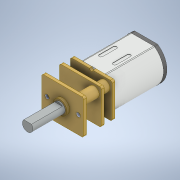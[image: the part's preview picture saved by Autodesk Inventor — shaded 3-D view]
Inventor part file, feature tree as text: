
AUTODESK INVENTOR PART (.ipt)
format: ipt  version: 2020 (Build 240168000, 168)  size: 244,224 bytes
history: native  units: mm
features: other x22, mirror x2
ambient origin geometry x8: Origin, YZ Plane, XZ Plane, XY Plane, X Axis, Y Axis, Z Axis, Center Point
bodies: Body1 (feature_tree), Body2 (feature_tree), Body3 (feature_tree), Body4 (feature_tree), Body5 (feature_tree), Body6 (feature_tree), Body7 (feature_tree), Body8 (feature_tree), Body9 (feature_tree), Body10 (feature_tree), Body11 (feature_tree), Body12 (feature_tree)
feature tree (24):
  other  "Твердое тело1"
  other  "Твердое тело2"
  other  "Твердое тело3"
  other  "Твердое тело4"
  other  "Твердое тело5"
  other  "Твердое тело6"
  other  "Твердое тело7"
  other  "Твердое тело8"
  other  "Твердое тело9"
  other  "Твердое тело10"
  other  "Твердое тело11"
  other  "Твердое тело12"
  other  "Cut-Extrude1"
  other  "Base-Flange2"
  mirror  "Mirror1"
  other  "Base-Flange4"
  other  "Boss-Extrude4[1]"
  other  "Boss-Extrude4[2]"
  other  "Boss-Extrude5[1]"
  other  "Boss-Extrude5[2]"
  other  "Cut-Extrude2"
  other  "M1.6 Tapped Hole1"
  other  "Cut-Extrude3"
  mirror  "Mirror2"
